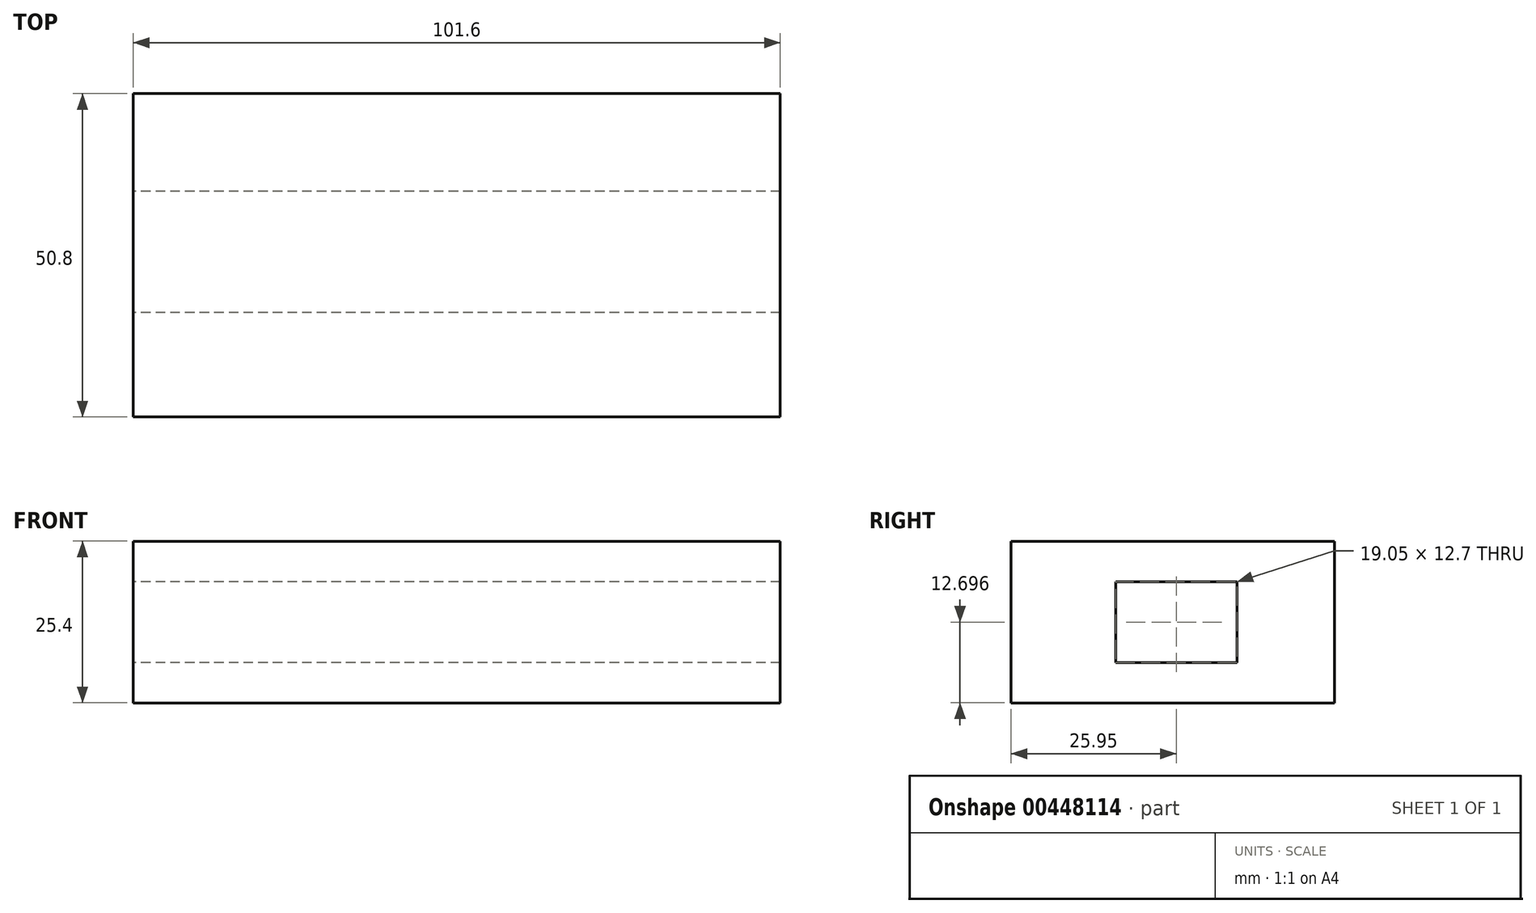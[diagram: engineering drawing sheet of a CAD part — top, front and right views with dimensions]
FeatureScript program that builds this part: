
annotation { "Feature Type Name" : "Feature", "Feature Type Description" : "" }
export const myFeature = defineFeature(function(context is Context, id is Id, definition is map)
    precondition{}
    {
        {
            var Q0;
            Q0=qCreatedBy(makeId("Right.planeOp"),FACE);
            var sketch = newSketch(context, id + "F0", { "sketchPlane" : qUnion([Q0])});
            skLineSegment(sketch, "E0.bottom", {"start": v(-25.95, -0.56) * mm, "end": v(24.85, -0.56) * mm});
            skLineSegment(sketch, "E0.top", {"start": v(-25.95, -25.96) * mm, "end": v(24.85, -25.96) * mm});
            skLineSegment(sketch, "E0.left", {"start": v(-25.95, -0.56) * mm, "end": v(-25.95, -25.96) * mm});
            skLineSegment(sketch, "E0.right", {"start": v(24.85, -0.56) * mm, "end": v(24.85, -25.96) * mm});
            skSolve(sketch);
        }
        {
            var Q0;
            Q0=makeQuery(id+"F0.imprint","IMPRINT",FACE,{"disambiguationData":[TD([[makeQuery(id+"F0.imprint","IMPRINT",EDGE,{"derivedFrom":sQuery(id+"F0.wireOp",EDGE,"E0.bottom")}),-1.0]])]});
            extrude(context, id + "F1", {"entities" : qUnion([Q0]), "endBound" : BoundingType.SYMMETRIC, "depth" : 101.6 * mm});
        }
        {
            var Q0;
            Q0=qCreatedBy(makeId("Right.planeOp"),FACE);
            var sketch = newSketch(context, id + "F2", { "sketchPlane" : qUnion([Q0])});
            skLineSegment(sketch, "E1.bottom", {"start": v(9.52, -19.61) * mm, "end": v(-9.53, -19.61) * mm});
            skLineSegment(sketch, "E1.top", {"start": v(9.53, -6.91) * mm, "end": v(-9.52, -6.91) * mm});
            skLineSegment(sketch, "E1.left", {"start": v(9.52, -19.61) * mm, "end": v(9.53, -6.91) * mm});
            skLineSegment(sketch, "E1.right", {"start": v(-9.53, -19.61) * mm, "end": v(-9.52, -6.91) * mm});
            skPoint(sketch, "E1.middle", {"position": v(0, -13.26) * mm});
            skSolve(sketch);
        }
        {
            var Q0;
            Q0 = qSketchRegion(id + "F2", true);
            extrude(context, id + "F3", {"entities" : qUnion([Q0]), "operationType" : NewBodyOperationType.REMOVE, "endBound" : BoundingType.SYMMETRIC, "depth" : 243.2 * mm});
        }
    });
